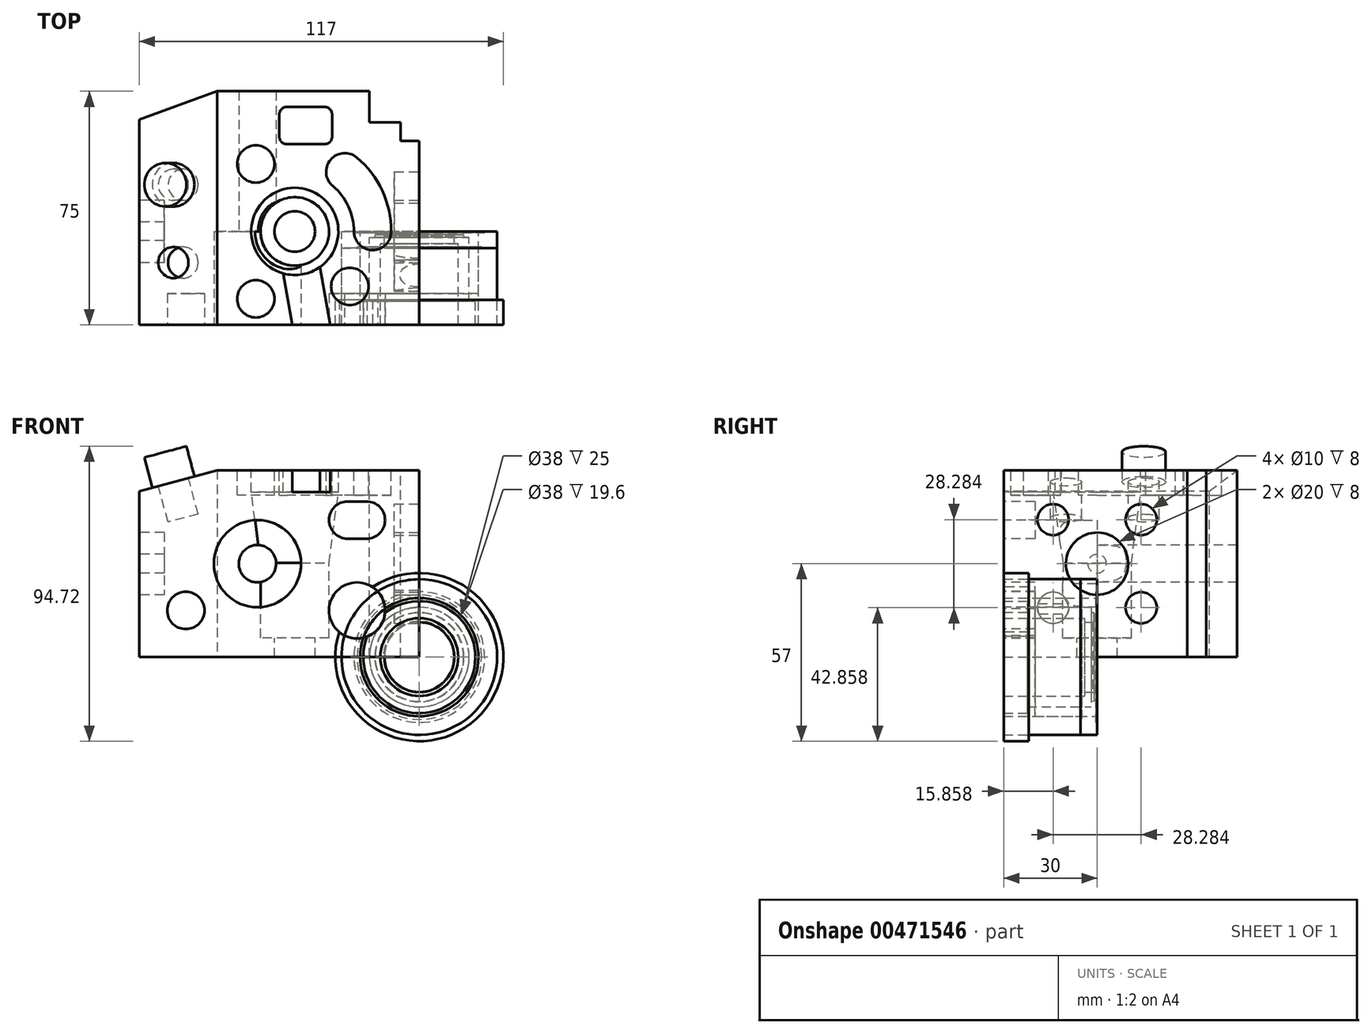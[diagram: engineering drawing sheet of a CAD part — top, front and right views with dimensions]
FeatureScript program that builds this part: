
annotation { "Feature Type Name" : "Feature", "Feature Type Description" : "" }
export const myFeature = defineFeature(function(context is Context, id is Id, definition is map)
    precondition{}
    {
        {
            var Q0;
            Q0=qCreatedBy(makeId("Top.planeOp"),FACE);
            var sketch = newSketch(context, id + "F0", { "sketchPlane" : qUnion([Q0])});
            skLineSegment(sketch, "E0", {"start": v(14.14, 0) * mm, "end": v(25, 0) * mm});
            skLineSegment(sketch, "E1", {"start": v(25, 0) * mm, "end": v(25, 30) * mm});
            skLineSegment(sketch, "E2", {"start": v(25, 30) * mm, "end": v(21, 30) * mm});
            skLineSegment(sketch, "E3", {"start": v(21, 30) * mm, "end": v(21, 29.6) * mm});
            skLineSegment(sketch, "E4", {"start": v(21, 29.6) * mm, "end": v(19, 29.6) * mm});
            skLineSegment(sketch, "E5", {"start": v(19, 29.6) * mm, "end": v(19, 10) * mm});
            skLineSegment(sketch, "E6", {"start": v(19, 10) * mm, "end": v(12.5, 10) * mm});
            skLineSegment(sketch, "E7", {"start": v(12.5, 10) * mm, "end": v(12.5, 0) * mm});
            skLineSegment(sketch, "E8", {"start": v(12.5, 0) * mm, "end": v(14.14, 0) * mm});
            skLineSegment(sketch, "E9", {"start": v(0, 44.63) * mm, "end": v(0, -7.3) * mm, "construction": true});
            skSolve(sketch);
        }
        {
            var Q0;
            Q0=makeQuery(id+"F0.imprint","IMPRINT",FACE,{"disambiguationData":[TD([[makeQuery(id+"F0.imprint","IMPRINT",EDGE,{"derivedFrom":sQuery(id+"F0.wireOp",EDGE,"E0")}),1.0]])]});
            var Q1;
            Q1=sQuery(id+"F0.wireOp",EDGE,"E9");
            revolve(context, id + "F1", {"entities" : qUnion([Q0]), "axis" : qUnion([Q1]), "revolveType" : RevolveType.FULL});
        }
        {
            var Q0;
            Q0=qCreatedBy(makeId("Top.planeOp"),FACE);
            var sketch = newSketch(context, id + "F2", { "sketchPlane" : qUnion([Q0])});
            skLineSegment(sketch, "E10", {"start": v(27, 0) * mm, "end": v(27, 8) * mm});
            skLineSegment(sketch, "E11", {"start": v(27, 8) * mm, "end": v(25, 8) * mm});
            skLineSegment(sketch, "E12", {"start": v(25, 8) * mm, "end": v(25, 24.69) * mm});
            skLineSegment(sketch, "E13", {"start": v(25, 24.69) * mm, "end": v(20, 24.6) * mm});
            skLineSegment(sketch, "E14", {"start": v(20, 24.6) * mm, "end": v(20, 25) * mm});
            skLineSegment(sketch, "E15", {"start": v(20, 25) * mm, "end": v(19, 25) * mm});
            skLineSegment(sketch, "E16", {"start": v(19, 25) * mm, "end": v(19, 0) * mm});
            skLineSegment(sketch, "E17", {"start": v(19, 0) * mm, "end": v(27, 0) * mm});
            skLineSegment(sketch, "E18", {"start": v(0, 33.85) * mm, "end": v(0, -6.26) * mm, "construction": true});
            skSolve(sketch);
        }
        {
            var Q0;
            Q0=makeQuery(id+"F2.imprint","IMPRINT",FACE,{"disambiguationData":[TD([[makeQuery(id+"F2.imprint","IMPRINT",EDGE,{"derivedFrom":sQuery(id+"F2.wireOp",EDGE,"E10")}),1.0]])]});
            var Q1;
            Q1=sQuery(id+"F2.wireOp",EDGE,"E18");
            revolve(context, id + "F3", {"entities" : qUnion([Q0]), "axis" : qUnion([Q1]), "revolveType" : RevolveType.FULL});
        }
        {
            var Q0;
            Q0=qCreatedBy(makeId("Top.planeOp"),FACE);
            var sketch = newSketch(context, id + "F4", { "sketchPlane" : qUnion([Q0])});
            skLineSegment(sketch, "E19", {"start": v(12.5, 0) * mm, "end": v(12.5, 26) * mm});
            skLineSegment(sketch, "E20", {"start": v(12.5, 26) * mm, "end": v(11.2, 26) * mm});
            skLineSegment(sketch, "E21", {"start": v(11.2, 26) * mm, "end": v(11.2, 28.58) * mm});
            skLineSegment(sketch, "E22", {"start": v(11.2, 28.58) * mm, "end": v(11.55, 29) * mm});
            skLineSegment(sketch, "E23", {"start": v(11.55, 29) * mm, "end": v(14.2, 28.98) * mm});
            skLineSegment(sketch, "E24", {"start": v(14.2, 28.98) * mm, "end": v(14.35, 28.08) * mm});
            skLineSegment(sketch, "E25", {"start": v(14.35, 28.08) * mm, "end": v(16, 28.08) * mm});
            skLineSegment(sketch, "E26", {"start": v(16, 28.08) * mm, "end": v(16, 7.6) * mm});
            skLineSegment(sketch, "E27", {"start": v(16, 7.6) * mm, "end": v(18, 7.6) * mm});
            skLineSegment(sketch, "E28", {"start": v(18, 7.6) * mm, "end": v(18, 0) * mm});
            skLineSegment(sketch, "E29", {"start": v(18, 0) * mm, "end": v(12.5, 0) * mm});
            skLineSegment(sketch, "E30", {"start": v(0, 33.6) * mm, "end": v(0, -1.9) * mm, "construction": true});
            skSolve(sketch);
        }
        {
            var Q0;
            Q0=makeQuery(id+"F4.imprint","IMPRINT",FACE,{"disambiguationData":[TD([[makeQuery(id+"F4.imprint","IMPRINT",EDGE,{"derivedFrom":sQuery(id+"F4.wireOp",EDGE,"E19")}),-1.0]])]});
            var Q1;
            Q1=sQuery(id+"F4.wireOp",EDGE,"E30");
            revolve(context, id + "F5", {"entities" : qUnion([Q0]), "axis" : qUnion([Q1]), "revolveType" : RevolveType.FULL});
        }
        {
            var Q0;
            Q0=qCreatedBy(makeId("Top.planeOp"),FACE);
            var sketch = newSketch(context, id + "F6", { "sketchPlane" : qUnion([Q0])});
            skLineSegment(sketch, "E31.bottom", {"start": v(0, 0) * mm, "end": v(-90, 0) * mm});
            skLineSegment(sketch, "E31.top", {"start": v(0, 75) * mm, "end": v(-90, 75) * mm});
            skLineSegment(sketch, "E31.left", {"start": v(0, 0) * mm, "end": v(0, 75) * mm});
            skLineSegment(sketch, "E31.right", {"start": v(-90, 0) * mm, "end": v(-90, 75) * mm});
            skSolve(sketch);
        }
        {
            var Q0;
            Q0 = qSketchRegion(id + "F6", true);
            extrude(context, id + "F7", {"entities" : qUnion([Q0]), "depth" : 60 * mm, "offsetDistance" : 25 * mm});
        }
        {
            var Q0;
            Q0=makeQuery(id+"F7.opExtrude","SWEPT_FACE",FACE,{"disambiguationData":[OSD([sQuery(id+"F6.wireOp",EDGE,"E31.bottom")])]});
            var sketch = newSketch(context, id + "F8", { "sketchPlane" : qUnion([Q0])});
            skLineSegment(sketch, "E32", {"start": v(-90, 53.3) * mm, "end": v(-65, 60) * mm});
            skSolve(sketch);
        }
        {
            var Q0;
            {var subQ0=sQuery(id+"F8.wireOp",EDGE,"E32");Q0=makeQuery(id+"F8.imprint","IMPRINT",FACE,{"disambiguationData":[TD([[makeQuery(id+"F8.imprint","IMPRINT",EDGE,{"derivedFrom":subQ0}),1.0]])]});}
            extrude(context, id + "F9", {"entities" : qUnion([Q0]), "operationType" : NewBodyOperationType.REMOVE, "endBound" : BoundingType.THROUGH_ALL, "oppositeDirection" : true, "depth" : 25 * mm, "offsetDistance" : 25 * mm});
        }
        {
            var Q0;
            Q0=makeQuery(id+"F7.opExtrude","CAP_FACE",FACE,{"disambiguationData":[OSD([sQuery(id+"F6.wireOp",EDGE,"E31.bottom"),sQuery(id+"F6.wireOp",EDGE,"E31.top"),sQuery(id+"F6.wireOp",EDGE,"E31.left"),sQuery(id+"F6.wireOp",EDGE,"E31.right")])],"isStart":false});
            var sketch = newSketch(context, id + "F10", { "sketchPlane" : qUnion([Q0])});
            skLineSegment(sketch, "E33", {"start": v(-16, 75) * mm, "end": v(-16, 65) * mm});
            skLineSegment(sketch, "E34", {"start": v(-16, 65) * mm, "end": v(-6, 65) * mm});
            skLineSegment(sketch, "E35", {"start": v(-6, 65) * mm, "end": v(-6, 59) * mm});
            skLineSegment(sketch, "E36", {"start": v(-6, 59) * mm, "end": v(0, 59) * mm});
            skSolve(sketch);
        }
        {
            var Q0;
            {var subQ1=sQuery(id+"F10.wireOp",EDGE,"E33");Q0=makeQuery(id+"F10.imprint","IMPRINT",FACE,{"disambiguationData":[TD([[makeQuery(id+"F10.imprint","IMPRINT",EDGE,{"derivedFrom":subQ1}),1.0]])]});}
            extrude(context, id + "F11", {"entities" : qUnion([Q0]), "operationType" : NewBodyOperationType.REMOVE, "endBound" : BoundingType.THROUGH_ALL, "oppositeDirection" : true, "depth" : 25 * mm, "offsetDistance" : 25 * mm});
        }
        {
            var Q0;
            Q0=qCreatedBy(makeId("Front.planeOp"),FACE);
            cPlane(context, id + "F12", {"entities" : qUnion([Q0]), "cplaneType" : CPlaneType.OFFSET, "offset" : 30 * mm, "oppositeDirection" : true, "width" : 150 * mm, "height" : 150 * mm});
        }
        {
            var Q0;
            Q0=qCreatedBy(id+"F12.planeOp",FACE);
            var sketch = newSketch(context, id + "F13", { "sketchPlane" : qUnion([Q0])});
            skLineSegment(sketch, "E37", {"start": v(-26, 60) * mm, "end": v(-26, 53) * mm});
            skLineSegment(sketch, "E38", {"start": v(-26, 53) * mm, "end": v(-29, 30.21) * mm});
            skLineSegment(sketch, "E39", {"start": v(-29, 30.21) * mm, "end": v(-29, 6.16) * mm});
            skLineSegment(sketch, "E40", {"start": v(-29, 6.16) * mm, "end": v(-40, 6.16) * mm});
            skLineSegment(sketch, "E41", {"start": v(-40, 6.16) * mm, "end": v(-40, 60) * mm});
            skLineSegment(sketch, "E42", {"start": v(-40, 60) * mm, "end": v(-26, 60) * mm});
            skSolve(sketch);
        }
        {
            var Q0;
            Q0=makeQuery(id+"F13.imprint","IMPRINT",FACE,{"disambiguationData":[TD([[makeQuery(id+"F13.imprint","IMPRINT",EDGE,{"derivedFrom":sQuery(id+"F13.wireOp",EDGE,"E37")}),-1.0]])]});
            var Q1;
            Q1=sQuery(id+"F13.wireOp",EDGE,"E41");
            revolve(context, id + "F14", {"operationType" : NewBodyOperationType.REMOVE, "entities" : qUnion([Q0]), "axis" : qUnion([Q1]), "revolveType" : RevolveType.FULL, "oppositeDirection" : true});
        }
        {
            var Q0;
            Q0=makeQuery(id+"F14.boolean.opBoolean","COPY",FACE,{"derivedFrom":makeQuery(id+"F14.opRevolve","SWEPT_FACE",FACE,{"disambiguationData":[OSD([sQuery(id+"F13.wireOp",EDGE,"E40")])]})});
            var sketch = newSketch(context, id + "F15", { "sketchPlane" : qUnion([Q0])});
            skCircle(sketch, "E43", {"center": v(-40, 30) * mm, "radius": 6.5 * mm});
            skSolve(sketch);
        }
        {
            var Q0;
            Q0=makeQuery(id+"F15.imprint","IMPRINT",FACE,{"disambiguationData":[TD([[makeQuery(id+"F15.imprint","IMPRINT",EDGE,{"derivedFrom":sQuery(id+"F15.wireOp",EDGE,"E43")}),1.0]])]});
            extrude(context, id + "F16", {"entities" : qUnion([Q0]), "operationType" : NewBodyOperationType.REMOVE, "endBound" : BoundingType.THROUGH_ALL, "oppositeDirection" : true, "depth" : 25 * mm, "offsetDistance" : 25 * mm});
        }
        {
            var Q0;
            Q0=makeQuery(id+"F7.opExtrude","CAP_FACE",FACE,{"disambiguationData":[OSD([sQuery(id+"F6.wireOp",EDGE,"E31.bottom"),sQuery(id+"F6.wireOp",EDGE,"E31.top"),sQuery(id+"F6.wireOp",EDGE,"E31.left"),sQuery(id+"F6.wireOp",EDGE,"E31.right")])],"isStart":false});
            var sketch = newSketch(context, id + "F17", { "sketchPlane" : qUnion([Q0])});
            skCircle(sketch, "E44", {"center": v(-40, 30) * mm, "radius": 25 * mm, "construction": true});
            skCircle(sketch, "E45", {"center": v(-22.32, 12.32) * mm, "radius": 6 * mm});
            skLineSegment(sketch, "E46", {"start": v(-40, 30) * mm, "end": v(-22.32, 12.32) * mm, "construction": true});
            skCircle(sketch, "E47", {"center": v(-52.5, 8.35) * mm, "radius": 6 * mm});
            skCircle(sketch, "E48", {"center": v(-52.5, 51.65) * mm, "radius": 6 * mm});
            skLineSegment(sketch, "E49", {"start": v(-40, 30) * mm, "end": v(-52.5, 51.65) * mm, "construction": true});
            skLineSegment(sketch, "E50", {"start": v(-40, 30) * mm, "end": v(-52.5, 8.35) * mm, "construction": true});
            skSolve(sketch);
        }
        {
            var Q0;
            Q0=makeQuery(id+"F17.imprint","IMPRINT",FACE,{"disambiguationData":[TD([[makeQuery(id+"F17.imprint","IMPRINT",EDGE,{"derivedFrom":sQuery(id+"F17.wireOp",EDGE,"E48")}),1.0]])]});
            var Q1;
            Q1=makeQuery(id+"F17.imprint","IMPRINT",FACE,{"disambiguationData":[TD([[makeQuery(id+"F17.imprint","IMPRINT",EDGE,{"derivedFrom":sQuery(id+"F17.wireOp",EDGE,"E47")}),1.0]])]});
            var Q2;
            Q2=makeQuery(id+"F17.imprint","IMPRINT",FACE,{"disambiguationData":[TD([[makeQuery(id+"F17.imprint","IMPRINT",EDGE,{"derivedFrom":sQuery(id+"F17.wireOp",EDGE,"E45")}),1.0]])]});
            extrude(context, id + "F18", {"entities" : qUnion([Q0, Q1, Q2]), "operationType" : NewBodyOperationType.REMOVE, "oppositeDirection" : true, "depth" : 8 * mm, "offsetDistance" : 25 * mm});
        }
        {
            var Q0;
            Q0=makeQuery(id+"F7.opExtrude","CAP_FACE",FACE,{"disambiguationData":[OSD([sQuery(id+"F6.wireOp",EDGE,"E31.bottom"),sQuery(id+"F6.wireOp",EDGE,"E31.top"),sQuery(id+"F6.wireOp",EDGE,"E31.left"),sQuery(id+"F6.wireOp",EDGE,"E31.right")])],"isStart":false});
            var sketch = newSketch(context, id + "F19", { "sketchPlane" : qUnion([Q0])});
            skLineSegment(sketch, "E51", {"start": v(-40, 30) * mm, "end": v(-34.71, 0) * mm, "construction": true});
            skLineSegment(sketch, "E52", {"start": v(-43.71, 16.5) * mm, "end": v(-40.8, 0) * mm});
            skLineSegment(sketch, "E53", {"start": v(-31.9, 18.58) * mm, "end": v(-28.62, 0) * mm});
            skSolve(sketch);
        }
        {
            var Q0;
            {var subQ0=sQuery(id+"F19.wireOp",EDGE,"E52");Q0=makeQuery(id+"F19.imprint","IMPRINT",FACE,{"disambiguationData":[TD([[makeQuery(id+"F19.imprint","IMPRINT",EDGE,{"derivedFrom":subQ0}),1.0]])]});}
            extrude(context, id + "F20", {"entities" : qUnion([Q0]), "operationType" : NewBodyOperationType.REMOVE, "oppositeDirection" : true, "depth" : 7 * mm, "offsetDistance" : 25 * mm});
        }
        {
            var Q0;
            Q0=makeQuery(id+"F7.opExtrude","CAP_FACE",FACE,{"disambiguationData":[OSD([sQuery(id+"F6.wireOp",EDGE,"E31.bottom"),sQuery(id+"F6.wireOp",EDGE,"E31.top"),sQuery(id+"F6.wireOp",EDGE,"E31.left"),sQuery(id+"F6.wireOp",EDGE,"E31.right")])],"isStart":true});
            var sketch = newSketch(context, id + "F21", { "sketchPlane" : qUnion([Q0])});
            skLineSegment(sketch, "E54", {"start": v(-90, -65.9) * mm, "end": v(-65, -75) * mm});
            skSolve(sketch);
        }
        {
            var Q0;
            {var subQ0=sQuery(id+"F21.wireOp",EDGE,"E54");Q0=makeQuery(id+"F21.imprint","IMPRINT",FACE,{"disambiguationData":[TD([[makeQuery(id+"F21.imprint","IMPRINT",EDGE,{"derivedFrom":subQ0}),-1.0]])]});}
            extrude(context, id + "F22", {"entities" : qUnion([Q0]), "operationType" : NewBodyOperationType.REMOVE, "endBound" : BoundingType.THROUGH_ALL, "oppositeDirection" : true, "depth" : 25 * mm, "offsetDistance" : 25 * mm});
        }
        {
            var Q0;
            Q0=makeQuery(id+"F7.opExtrude","CAP_FACE",FACE,{"disambiguationData":[OSD([sQuery(id+"F6.wireOp",EDGE,"E31.bottom"),sQuery(id+"F6.wireOp",EDGE,"E31.top"),sQuery(id+"F6.wireOp",EDGE,"E31.left"),sQuery(id+"F6.wireOp",EDGE,"E31.right")])],"isStart":false});
            var sketch = newSketch(context, id + "F23", { "sketchPlane" : qUnion([Q0])});
            skLineSegment(sketch, "E55.bottom", {"start": v(-30.5, 58) * mm, "end": v(-42.5, 58) * mm});
            skLineSegment(sketch, "E55.top", {"start": v(-30.5, 70) * mm, "end": v(-42.5, 70) * mm});
            skLineSegment(sketch, "E55.left", {"start": v(-28, 60.5) * mm, "end": v(-28, 67.5) * mm});
            skLineSegment(sketch, "E55.right", {"start": v(-45, 60.5) * mm, "end": v(-45, 67.5) * mm});
            skPoint(sketch, "E55.middle", {"position": v(-36.5, 64) * mm});
            skPoint(sketch, "E56.visualSharp", {"position": v(-45, 70) * mm});
            skArc(sketch, "E56.filletArc", {"start": v(-42.5, 70) * mm, "mid": v(-44.27, 69.27) * mm, "end": v(-45, 67.5) * mm});
            skPoint(sketch, "E57.visualSharp", {"position": v(-45, 58) * mm});
            skArc(sketch, "E57.filletArc", {"start": v(-45, 60.5) * mm, "mid": v(-44.27, 58.73) * mm, "end": v(-42.5, 58) * mm});
            skPoint(sketch, "E58.visualSharp", {"position": v(-28, 58) * mm});
            skArc(sketch, "E58.filletArc", {"start": v(-30.5, 58) * mm, "mid": v(-28.73, 58.73) * mm, "end": v(-28, 60.5) * mm});
            skPoint(sketch, "E59.visualSharp", {"position": v(-28, 70) * mm});
            skArc(sketch, "E59.filletArc", {"start": v(-28, 67.5) * mm, "mid": v(-28.73, 69.27) * mm, "end": v(-30.5, 70) * mm});
            skSolve(sketch);
        }
        {
            var Q0;
            Q0=makeQuery(id+"F23.imprint","IMPRINT",FACE,{"disambiguationData":[TD([[makeQuery(id+"F23.imprint","IMPRINT",EDGE,{"derivedFrom":sQuery(id+"F23.wireOp",EDGE,"E55.bottom")}),-1.0]])]});
            extrude(context, id + "F24", {"entities" : qUnion([Q0]), "operationType" : NewBodyOperationType.REMOVE, "oppositeDirection" : true, "depth" : 8 * mm, "offsetDistance" : 25 * mm});
        }
        {
            var Q0;
            {var subQ3=sQuery(id+"F8.wireOp",EDGE,"E32");Q0=makeQuery(id+"F8.imprint","IMPRINT",FACE,{"disambiguationData":[TD([[makeQuery(id+"F8.imprint","IMPRINT",EDGE,{"derivedFrom":subQ3}),-1.0]])]});}
            var sketch = newSketch(context, id + "F25", { "sketchPlane" : qUnion([Q0])});
            skLineSegment(sketch, "E60.bottom", {"start": v(-17, 38) * mm, "end": v(-23, 38) * mm});
            skLineSegment(sketch, "E60.top", {"start": v(-17, 50) * mm, "end": v(-23, 50) * mm});
            skPoint(sketch, "E60.middle", {"position": v(-20, 44) * mm});
            skArc(sketch, "E61", {"start": v(-23, 50) * mm, "mid": v(-29, 44) * mm, "end": v(-23, 38) * mm});
            skArc(sketch, "E62", {"start": v(-17, 50) * mm, "mid": v(-11, 44) * mm, "end": v(-17, 38) * mm});
            skSolve(sketch);
        }
        {
            var Q0;
            Q0 = qSketchRegion(id + "F25", true);
            extrude(context, id + "F26", {"entities" : qUnion([Q0]), "operationType" : NewBodyOperationType.REMOVE, "oppositeDirection" : true, "depth" : 10 * mm, "offsetDistance" : 25 * mm});
        }
        {
            var Q0;
            Q0=makeQuery(id+"F7.opExtrude","CAP_FACE",FACE,{"disambiguationData":[OSD([sQuery(id+"F6.wireOp",EDGE,"E31.bottom"),sQuery(id+"F6.wireOp",EDGE,"E31.top"),sQuery(id+"F6.wireOp",EDGE,"E31.left"),sQuery(id+"F6.wireOp",EDGE,"E31.right")])],"isStart":false});
            var sketch = newSketch(context, id + "F27", { "sketchPlane" : qUnion([Q0])});
            skCircle(sketch, "E63", {"center": v(-40, 30) * mm, "radius": 25 * mm, "construction": true});
            skArc(sketch, "E64", {"start": v(-21, 30) * mm, "mid": v(-22.78, 38.03) * mm, "end": v(-27.79, 44.55) * mm});
            skArc(sketch, "E65", {"start": v(-9, 30) * mm, "mid": v(-11.9, 43.1) * mm, "end": v(-20.07, 53.75) * mm});
            skLineSegment(sketch, "E66", {"start": v(-40, 30) * mm, "end": v(-6.04, 30) * mm, "construction": true});
            skLineSegment(sketch, "E67", {"start": v(-40, 30) * mm, "end": v(-19.17, 54.82) * mm, "construction": true});
            skArc(sketch, "E68", {"start": v(-21, 30) * mm, "mid": v(-15, 24) * mm, "end": v(-9, 30) * mm});
            skArc(sketch, "E69", {"start": v(-27.79, 44.55) * mm, "mid": v(-28.53, 53) * mm, "end": v(-20.07, 53.75) * mm});
            skSolve(sketch);
        }
        {
            var Q0;
            Q0=makeQuery(id+"F27.imprint","IMPRINT",FACE,{"disambiguationData":[TD([[makeQuery(id+"F27.imprint","IMPRINT",EDGE,{"derivedFrom":sQuery(id+"F27.wireOp",EDGE,"E64")}),-1.0]])]});
            extrude(context, id + "F28", {"entities" : qUnion([Q0]), "operationType" : NewBodyOperationType.REMOVE, "oppositeDirection" : true, "depth" : 8 * mm, "offsetDistance" : 25 * mm});
        }
        {
            var Q0;
            {var subQ3=sQuery(id+"F8.wireOp",EDGE,"E32");Q0=makeQuery(id+"F8.imprint","IMPRINT",FACE,{"disambiguationData":[TD([[makeQuery(id+"F8.imprint","IMPRINT",EDGE,{"derivedFrom":subQ3}),-1.0]])]});}
            var sketch = newSketch(context, id + "F29", { "sketchPlane" : qUnion([Q0])});
            skCircle(sketch, "E70", {"center": v(-20, 15) * mm, "radius": 9 * mm});
            skSolve(sketch);
        }
        {
            var Q0;
            Q0 = qSketchRegion(id + "F29", true);
            extrude(context, id + "F30", {"entities" : qUnion([Q0]), "operationType" : NewBodyOperationType.REMOVE, "oppositeDirection" : true, "depth" : 10 * mm, "offsetDistance" : 25 * mm});
        }
        {
            var Q0;
            {var subQ3=sQuery(id+"F8.wireOp",EDGE,"E32");Q0=makeQuery(id+"F8.imprint","IMPRINT",FACE,{"disambiguationData":[TD([[makeQuery(id+"F8.imprint","IMPRINT",EDGE,{"derivedFrom":subQ3}),-1.0]])]});}
            var sketch = newSketch(context, id + "F31", { "sketchPlane" : qUnion([Q0])});
            skCircle(sketch, "E71", {"center": v(-52, 30) * mm, "radius": 6 * mm});
            skCircle(sketch, "E72", {"center": v(-52, 30) * mm, "radius": 14 * mm});
            skSolve(sketch);
        }
        {
            var Q0;
            Q0 = qSketchRegion(id + "F31", true);
            extrude(context, id + "F32", {"entities" : qUnion([Q0]), "operationType" : NewBodyOperationType.REMOVE, "oppositeDirection" : true, "depth" : 30 * mm, "offsetDistance" : 25 * mm});
        }
        {
            var Q0;
            Q0=makeQuery(id+"F32.boolean.opBoolean","SPLIT",FACE,{"disambiguationData":[TD([makeQuery(id+"F32.opExtrude","SWEPT_FACE",FACE,{"disambiguationData":[OSD([sQuery(id+"F31.wireOp",EDGE,"E71")])]})])],"derivedFrom":makeQuery(id+"F7.opExtrude","SWEPT_FACE",FACE,{"disambiguationData":[OSD([sQuery(id+"F6.wireOp",EDGE,"E31.bottom")])]})});
            extrude(context, id + "F33", {"entities" : qUnion([Q0]), "operationType" : NewBodyOperationType.REMOVE, "endBound" : BoundingType.THROUGH_ALL, "oppositeDirection" : true, "depth" : 25 * mm, "offsetDistance" : 25 * mm});
        }
        {
            var Q0;
            {var subQ3=sQuery(id+"F6.wireOp",EDGE,"E31.left");var subQ5=sQuery(id+"F6.wireOp",EDGE,"E31.bottom");Q0=makeQuery(id+"F32.boolean.opBoolean","SPLIT",FACE,{"disambiguationData":[TD([makeQuery(id+"F7.opExtrude","SWEPT_FACE",FACE,{"disambiguationData":[OSD([subQ3])]})])],"derivedFrom":makeQuery(id+"F7.opExtrude","SWEPT_FACE",FACE,{"disambiguationData":[OSD([subQ5])]})});}
            var sketch = newSketch(context, id + "F34", { "sketchPlane" : qUnion([Q0])});
            skCircle(sketch, "E73", {"center": v(-75, 15) * mm, "radius": 6 * mm});
            skSolve(sketch);
        }
        {
            var Q0;
            Q0 = qSketchRegion(id + "F34", true);
            extrude(context, id + "F35", {"entities" : qUnion([Q0]), "operationType" : NewBodyOperationType.REMOVE, "oppositeDirection" : true, "depth" : 10 * mm, "offsetDistance" : 25 * mm});
        }
        {
            var Q0;
            Q0=makeQuery(id+"F7.opExtrude","SWEPT_FACE",FACE,{"disambiguationData":[OSD([sQuery(id+"F6.wireOp",EDGE,"E31.right")])]});
            var sketch = newSketch(context, id + "F36", { "sketchPlane" : qUnion([Q0])});
            skCircle(sketch, "E74", {"center": v(-30, 30) * mm, "radius": 10 * mm});
            skCircle(sketch, "E75", {"center": v(-30, 30) * mm, "radius": 3 * mm});
            skSolve(sketch);
        }
        {
            var Q0;
            Q0=makeQuery(id+"F36.imprint","IMPRINT",FACE,{"disambiguationData":[TD([[makeQuery(id+"F36.imprint","IMPRINT",EDGE,{"derivedFrom":sQuery(id+"F36.wireOp",EDGE,"E74")}),1.0]])]});
            extrude(context, id + "F37", {"entities" : qUnion([Q0]), "operationType" : NewBodyOperationType.REMOVE, "oppositeDirection" : true, "depth" : 8 * mm, "offsetDistance" : 25 * mm});
        }
        {
            var Q0;
            Q0=makeQuery(id+"F7.opExtrude","SWEPT_FACE",FACE,{"disambiguationData":[OSD([sQuery(id+"F6.wireOp",EDGE,"E31.left")])]});
            var sketch = newSketch(context, id + "F38", { "sketchPlane" : qUnion([Q0])});
            skCircle(sketch, "E76", {"center": v(30, 30) * mm, "radius": 10 * mm});
            skCircle(sketch, "E77", {"center": v(30, 30) * mm, "radius": 20 * mm, "construction": true});
            skLineSegment(sketch, "E78", {"start": v(30, 30) * mm, "end": v(46.83, 46.83) * mm, "construction": true});
            skLineSegment(sketch, "E79", {"start": v(30, 30) * mm, "end": v(56.7, 30) * mm, "construction": true});
            skCircle(sketch, "E80", {"center": v(44.14, 44.14) * mm, "radius": 5 * mm});
            skCircle(sketch, "E81.1.0", {"center": v(44.14, 15.86) * mm, "radius": 5 * mm});
            skCircle(sketch, "E81.2.0", {"center": v(15.86, 15.86) * mm, "radius": 5 * mm});
            skCircle(sketch, "E81.3.0", {"center": v(15.86, 44.14) * mm, "radius": 5 * mm});
            skLineSegment(sketch, "E81.anchor1", {"start": v(30, 30) * mm, "end": v(44.14, 44.14) * mm, "construction": true});
            skLineSegment(sketch, "E81.anchor2", {"start": v(30, 30) * mm, "end": v(15.86, 44.14) * mm, "construction": true});
            skSolve(sketch);
        }
        {
            var Q0;
            Q0=makeQuery(id+"F38.imprint","IMPRINT",FACE,{"disambiguationData":[TD([[makeQuery(id+"F38.imprint","IMPRINT",EDGE,{"derivedFrom":sQuery(id+"F38.wireOp",EDGE,"E76")}),1.0]])]});
            var Q1;
            Q1=makeQuery(id+"F38.imprint","IMPRINT",FACE,{"disambiguationData":[TD([[makeQuery(id+"F38.imprint","IMPRINT",EDGE,{"derivedFrom":sQuery(id+"F38.wireOp",EDGE,"E81.3.0")}),1.0]])]});
            var Q2;
            Q2=makeQuery(id+"F38.imprint","IMPRINT",FACE,{"disambiguationData":[TD([[makeQuery(id+"F38.imprint","IMPRINT",EDGE,{"derivedFrom":sQuery(id+"F38.wireOp",EDGE,"E80")}),1.0]])]});
            var Q3;
            Q3=makeQuery(id+"F38.imprint","IMPRINT",FACE,{"disambiguationData":[TD([[makeQuery(id+"F38.imprint","IMPRINT",EDGE,{"derivedFrom":sQuery(id+"F38.wireOp",EDGE,"E81.1.0")}),1.0]])]});
            var Q4;
            Q4=makeQuery(id+"F38.imprint","IMPRINT",FACE,{"disambiguationData":[TD([[makeQuery(id+"F38.imprint","IMPRINT",EDGE,{"derivedFrom":sQuery(id+"F38.wireOp",EDGE,"E81.2.0")}),1.0]])]});
            extrude(context, id + "F39", {"entities" : qUnion([Q0, Q1, Q2, Q3, Q4]), "operationType" : NewBodyOperationType.REMOVE, "oppositeDirection" : true, "depth" : 8 * mm, "offsetDistance" : 25 * mm});
        }
        {
            var Q0;
            Q0=makeQuery(id+"F9.boolean.opBoolean","COPY",FACE,{"derivedFrom":makeQuery(id+"F9.opExtrude","SWEPT_FACE",FACE,{"disambiguationData":[OSD([sQuery(id+"F8.wireOp",EDGE,"E32")])]})});
            var sketch = newSketch(context, id + "F40", { "sketchPlane" : qUnion([Q0])});
            skLineSegment(sketch, "E82", {"start": v(-61.75, 0) * mm, "end": v(-61.75, 52.15) * mm, "construction": true});
            skCircle(sketch, "E83", {"center": v(-61.75, 20) * mm, "radius": 5 * mm});
            skCircle(sketch, "E84", {"center": v(-61.75, 45) * mm, "radius": 5 * mm});
            skCircle(sketch, "E85", {"center": v(-61.75, 45) * mm, "radius": 7 * mm});
            skSolve(sketch);
        }
        {
            var Q0;
            Q0=makeQuery(id+"F40.imprint","IMPRINT",FACE,{"disambiguationData":[TD([[makeQuery(id+"F40.imprint","IMPRINT",EDGE,{"derivedFrom":sQuery(id+"F40.wireOp",EDGE,"E84")}),1.0]])]});
            var Q1;
            Q1=makeQuery(id+"F40.imprint","IMPRINT",FACE,{"disambiguationData":[TD([[makeQuery(id+"F40.imprint","IMPRINT",EDGE,{"derivedFrom":sQuery(id+"F40.wireOp",EDGE,"E83")}),1.0]])]});
            extrude(context, id + "F41", {"entities" : qUnion([Q0, Q1]), "operationType" : NewBodyOperationType.REMOVE, "oppositeDirection" : true, "depth" : 12 * mm, "offsetDistance" : 25 * mm});
        }
        {
            var Q0;
            Q0=makeQuery(id+"F40.imprint","IMPRINT",FACE,{"disambiguationData":[TD([[makeQuery(id+"F40.imprint","IMPRINT",EDGE,{"derivedFrom":sQuery(id+"F40.wireOp",EDGE,"E84")}),-1.0]])]});
            extrude(context, id + "F42", {"entities" : qUnion([Q0]), "operationType" : NewBodyOperationType.ADD, "depth" : 10 * mm, "offsetDistance" : 25 * mm});
        }
        {
            var Q0;
            Q0=makeQuery(id+"F40.imprint","IMPRINT",FACE,{"disambiguationData":[TD([[makeQuery(id+"F40.imprint","IMPRINT",EDGE,{"derivedFrom":sQuery(id+"F40.wireOp",EDGE,"E84")}),1.0]])]});
            extrude(context, id + "F43", {"entities" : qUnion([Q0]), "operationType" : NewBodyOperationType.ADD, "depth" : 10 * mm, "offsetDistance" : 25 * mm});
        }
    });
